# Revit family: Rodapié biselado
name_source: partatom
category: Perfiles
revit_build: Autodesk Revit 2015 (Build: 20140323_1530(x64)
units: mm (PartAtom-declared; Revit-internal decimal feet)

## types (9) — shared parameters

## per-type parameters (varying)
| type | Altura rodapié | Bisel | Grosor rodapié |
| Rodapié biselado 70×20 | 70 mm  [stored 0.229659 ft] | 10 mm  [stored 0.0328084 ft] | 20 mm  [stored 0.0656168 ft] |
| Rodapié biselado 100×20 | 100 mm  [stored 0.328084 ft] | 10 mm  [stored 0.0328084 ft] | 20 mm  [stored 0.0656168 ft] |
| Rodapié biselado 100×10 | 100 mm  [stored 0.328084 ft] | 5 mm  [stored 0.0164042 ft] | 10 mm  [stored 0.0328084 ft] |
| Rodapié biselado 50×20 | 50 mm | 10 mm  [stored 0.0328084 ft] | 20 mm  [stored 0.0656168 ft] |
| Rodapié biselado 50×10 | 50 mm | 5 mm  [stored 0.0164042 ft] | 10 mm  [stored 0.0328084 ft] |
| Rodapié biselado 70×10 | 70 mm  [stored 0.229659 ft] | 5 mm  [stored 0.0164042 ft] | 10 mm  [stored 0.0328084 ft] |
| Rodapié biselado 100×15 | 100 mm  [stored 0.328084 ft] | 8 mm  [stored 0.0262467 ft] | 15 mm |
| Rodapié biselado 70×15 | 70 mm  [stored 0.229659 ft] | 8 mm  [stored 0.0262467 ft] | 15 mm |
| Rodapié biselado 50×15 | 50 mm | 8 mm  [stored 0.0262467 ft] | 15 mm |

note: [stored X ft] marks values corroborated as IEEE doubles in the binary element streams (Revit-internal decimal feet)

## geometry (parser evidence)
native form markers: Blend x3
no freeform markers — native parametric forms only
